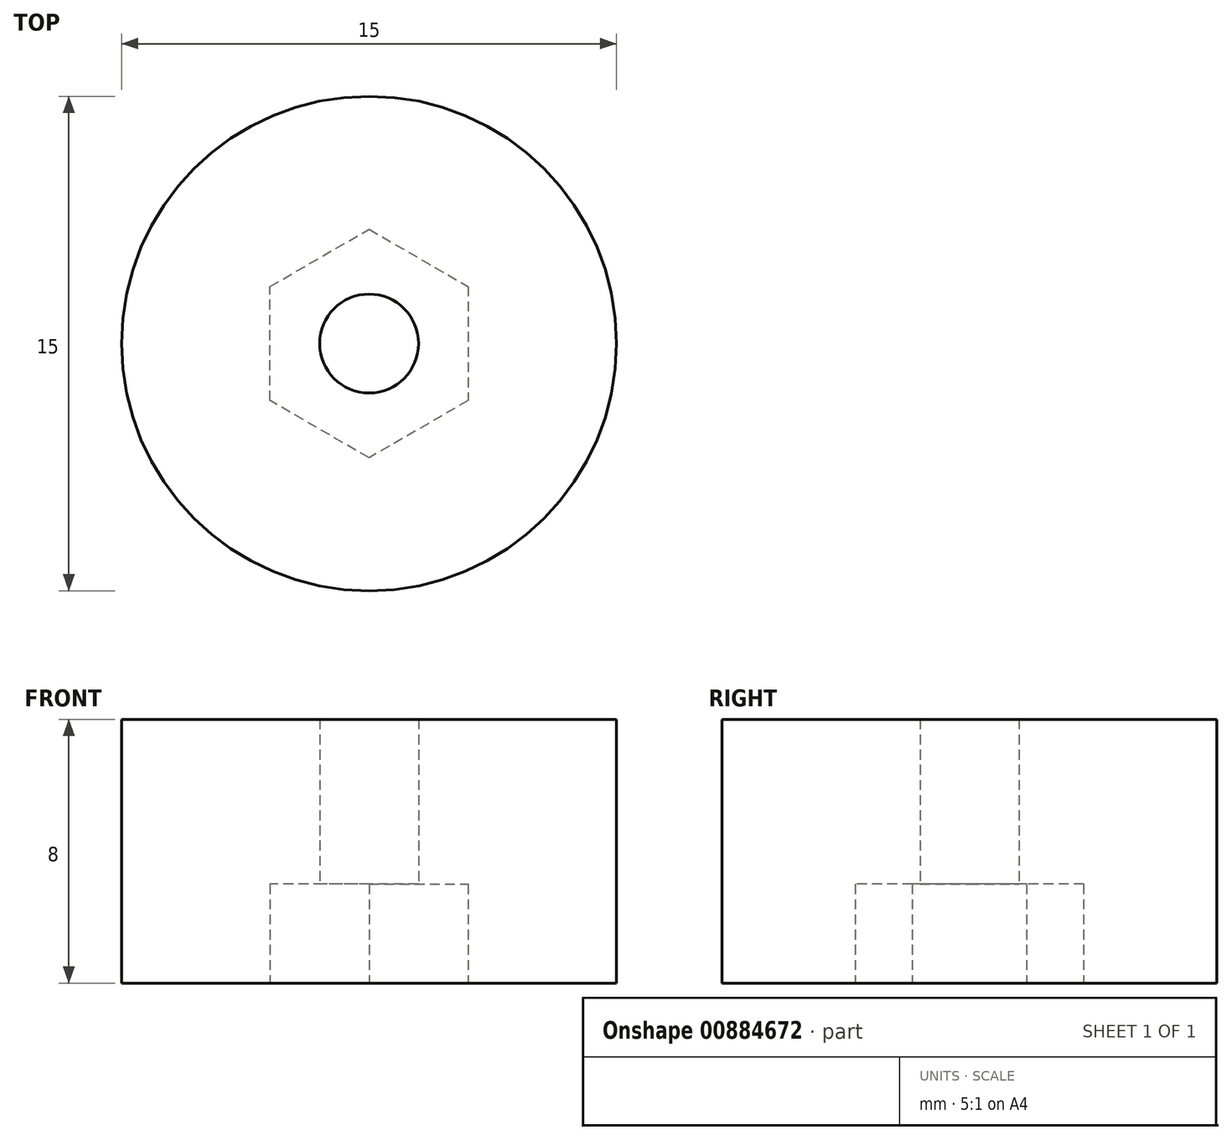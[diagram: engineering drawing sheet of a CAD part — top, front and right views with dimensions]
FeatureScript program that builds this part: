
annotation { "Feature Type Name" : "Feature", "Feature Type Description" : "" }
export const myFeature = defineFeature(function(context is Context, id is Id, definition is map)
    precondition{}
    {
        {
            var Q0;
            Q0=qCreatedBy(makeId("Top.planeOp"),FACE);
            var sketch = newSketch(context, id + "F0", { "sketchPlane" : qUnion([Q0])});
            skCircle(sketch, "E0", {"center": v(7.5, 7.5) * mm, "radius": 1.5 * mm});
            skCircle(sketch, "E1.cCircle", {"center": v(7.5, 7.5) * mm, "radius": 3 * mm, "construction": true});
            skLineSegment(sketch, "E1.0", {"start": v(10.5, 9.23) * mm, "end": v(10.5, 5.77) * mm});
            skLineSegment(sketch, "E1.1", {"start": v(10.5, 5.77) * mm, "end": v(7.5, 4.04) * mm});
            skLineSegment(sketch, "E1.2", {"start": v(7.5, 4.04) * mm, "end": v(4.5, 5.77) * mm});
            skLineSegment(sketch, "E1.3", {"start": v(4.5, 5.77) * mm, "end": v(4.5, 9.23) * mm});
            skLineSegment(sketch, "E1.4", {"start": v(4.5, 9.23) * mm, "end": v(7.5, 10.96) * mm});
            skLineSegment(sketch, "E1.5", {"start": v(7.5, 10.96) * mm, "end": v(10.5, 9.23) * mm});
            skPoint(sketch, "E1.0.midPoint", {"position": v(10.5, 7.5) * mm});
            skPoint(sketch, "E2", {"position": v(4.5, 7.5) * mm});
            skCircle(sketch, "E3", {"center": v(7.5, 7.5) * mm, "radius": 7.5 * mm});
            skLineSegment(sketch, "E4", {"start": v(0, 0) * mm, "end": v(0, 7.5) * mm, "construction": true});
            skLineSegment(sketch, "E5", {"start": v(0, 7.5) * mm, "end": v(7.5, 7.5) * mm, "construction": true});
            skSolve(sketch);
        }
        {
            var Q0;
            Q0=makeQuery(id+"F0.imprint","IMPRINT",FACE,{"disambiguationData":[TD([[makeQuery(id+"F0.imprint","IMPRINT",EDGE,{"derivedFrom":sQuery(id+"F0.wireOp",EDGE,"E1.0")}),1.0]])]});
            extrude(context, id + "F1", {"entities" : qUnion([Q0]), "depth" : 3 * mm, "offsetDistance" : 25 * mm});
        }
        {
            var Q0;
            Q0=makeQuery(id+"F1.opExtrude","CAP_FACE",FACE,{"disambiguationData":[OSD([sQuery(id+"F0.wireOp",EDGE,"E1.0"),sQuery(id+"F0.wireOp",EDGE,"E1.1"),sQuery(id+"F0.wireOp",EDGE,"E1.2"),sQuery(id+"F0.wireOp",EDGE,"E1.3"),sQuery(id+"F0.wireOp",EDGE,"E1.4"),sQuery(id+"F0.wireOp",EDGE,"E1.5"),sQuery(id+"F0.wireOp",EDGE,"E3")])],"isStart":false});
            var sketch = newSketch(context, id + "F2", { "sketchPlane" : qUnion([Q0])});
            skCircle(sketch, "E6.0", {"center": v(7.5, 7.5) * mm, "radius": 7.5 * mm});
            skSolve(sketch);
        }
        {
            var Q0;
            Q0=makeQuery(id+"F2.imprint","IMPRINT",FACE,{"disambiguationData":[TD([[makeQuery(id+"F2.imprint","IMPRINT",EDGE,{"derivedFrom":makeQuery(id+"F1.opExtrude","CAP_EDGE",EDGE,{"disambiguationData":[OSD([sQuery(id+"F0.wireOp",EDGE,"E1.0")])],"isStart":false})}),-1.0]])]});
            var Q1;
            Q1=makeQuery(id+"F2.imprint","IMPRINT",FACE,{"disambiguationData":[TD([[makeQuery(id+"F2.imprint","IMPRINT",EDGE,{"derivedFrom":sQuery(id+"F2.wireOp",EDGE,"E6.0")}),1.0]])]});
            extrude(context, id + "F3", {"entities" : qUnion([Q0, Q1]), "operationType" : NewBodyOperationType.ADD, "depth" : 5 * mm, "offsetDistance" : 25 * mm});
        }
        {
            var Q0;
            Q0=makeQuery(id+"F0.imprint","IMPRINT",FACE,{"disambiguationData":[TD([[makeQuery(id+"F0.imprint","IMPRINT",EDGE,{"derivedFrom":sQuery(id+"F0.wireOp",EDGE,"E0")}),1.0]])]});
            extrude(context, id + "F4", {"entities" : qUnion([Q0]), "operationType" : NewBodyOperationType.REMOVE, "depth" : 25 * mm, "offsetDistance" : 25 * mm});
        }
    });
